# Revit family: Fountain-Eyewash-Bradley_Corp-S19345
name_source: partatom
category: Plumbing Fixtures
units: mm (PartAtom-declared; Revit-internal decimal feet)

## family parameters
Cut with Voids When Loaded = No
Host = Face
Part Type = Normal
Room Calculation Point = No
Round Connector Dimension = Use Radius
Shared = No

## types (1)
- S19-345
    Assembly Code = D2010700
    Barrier-Free = Yes
    Buy American Act = To Be Determined
    Cold Water Connection Diameter = 1"
    Cold Water Connection Radius = 1"
    Default Elevation = 0 "
    Depth = 4 "
    Description = Barrier-Free Recessed Drench Shower and Eyewash
    Fixture Material = Metal - Bradley Corp - Stainless Steel
    Industry Standards = Complies with ANSI Standard Z358.1-2009
    Installation Type = Recessed Wall Mounted
    Length = 33.625 "
    Low Emitting Material = No
    Manufacturer = Bradley Corporation
    Manufacturer Installation URL - English = https://www.bradleycorp.com
    MasterFormat Number = 22.45.00
    MasterFormat Title = Emergency Plumbing Fixtures
    Model = S19345
    Navigator EFX25 Emergency Thermostat Mixing Valve = No
    OmniClass Code = 23.29.37.13
    OmniClass Title = Emergency Eye Wash Stations
    Percentage of Recycled Content = 0
    Pipe Fitting Material = Metal - Bradley Corp - Stainless Steel
    Product Tech Data URL - English = https://www.bradleycorp.com
    Showerhead Material = Plastic - Bradley Corp - Safety Yellow
    URL = https://www.bradleycorp.com
    Version = 1.0
    Warranty Information = View Product Warranty on Product Page
    Waste Water Connection Diameter = 1"
    Waste Water Connection Radius = 1"
    Width = 27.625 "

## geometry (parser evidence)
native form markers: Blend x22, Sweep x3
no freeform markers — native parametric forms only
